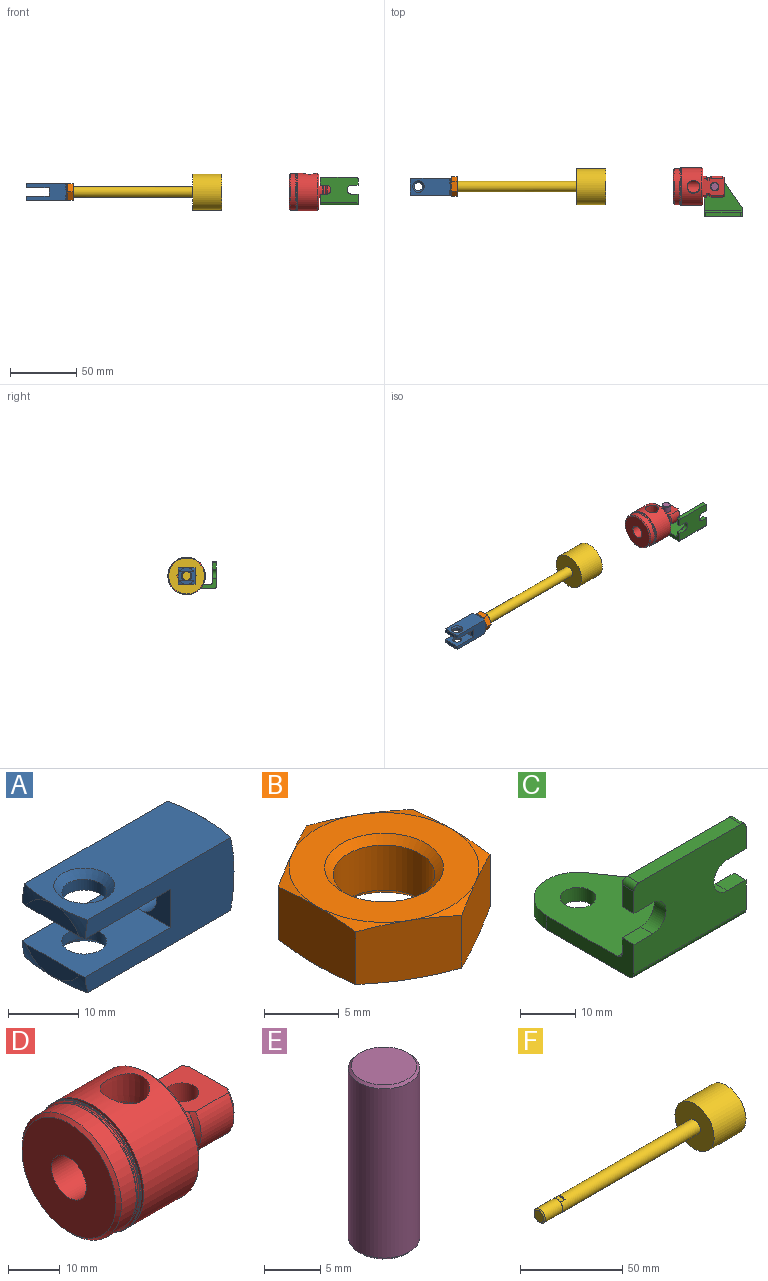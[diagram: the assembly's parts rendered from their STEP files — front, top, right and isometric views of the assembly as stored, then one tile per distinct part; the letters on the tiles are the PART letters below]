
ASSEMBLY  parts=6 mates=5
PART A: 27 faces, bbox 30.5x18.3x18.3 mm
  f0: torus R=3.17mm, axis (1,0,0), area 8.9mm2, adj f3,f5,f9
  f1: plane 30.35x13.05mm, normal (0,-1,0), area 262.9mm2, adj f2,f3,f4,f8,f14,f18,f20,f21
  f2: plane 17.51x12.73mm, normal (0,0,-1), area 189.7mm2, adj f1,f5,f15,f16,f17,f18,f21,f22
  f3: plane 30.18x12.7mm, normal (0,0,1), area 319.9mm2, adj f0,f1,f5,f13,f21,f22,f23
  f4: plane 30.18x12.7mm, normal (0,0,-1), area 319.9mm2, adj f1,f5,f6,f14,f19,f20,f24
  f5: plane 30.35x13.05mm, normal (0,1,0), area 261.5mm2, adj f0,f2,f3,f4,f8,f17,f19,f22
  f6: cone r=3.19mm half-angle=45deg, axis (0,0,-1), area 38.2mm2, adj f4,f7
  f7: cylinder r=3.19mm len=6.39mm, axis (0,0,1), area 37.6mm2, adj f6,f8
  f8: plane 17.51x12.73mm, normal (0,0,1), area 189.7mm2, adj f1,f5,f7,f12,f17,f18,f19,f20
  f9: plane 12.7x12.7mm, normal (1,0,0), area 77.2mm2, adj f0,f11,f14,f23,f24
  f10: cylinder r=3.4mm len=12.13mm, axis (-1,0,0), area 258.8mm2, adj f11,f12,f16,f17,f18
  f11: cone r=3.4mm half-angle=45deg, axis (1,0,0), area 18.7mm2, adj f9,f10
  f12: plane 1.29x0.06mm, normal (1,0,0), area 0.1mm2, adj f8,f10
  f13: cone r=4.34mm half-angle=45deg, axis (0,0,1), area 38.2mm2, adj f3,f15
  f14: torus R=3.17mm, axis (1,0,0), area 8.9mm2, adj f1,f4,f9
  f15: cylinder r=3.19mm len=6.39mm, axis (0,0,1), area 37.6mm2, adj f2,f13
  f16: plane 1.29x0.06mm, normal (1,0,0), area 0.1mm2, adj f2,f10
  f17: plane 6.67x5.7mm, normal (-1,0,0), area 24.3mm2, adj f2,f5,f8,f10
  f18: plane 6.67x5.7mm, normal (-1,0,0), area 24.3mm2, adj f1,f2,f8,f10
  f19: torus R=3.17mm, axis (1,0,0), area 8.2mm2, adj f4,f5,f8,f25
  f20: torus R=3.17mm, axis (1,0,0), area 8.2mm2, adj f1,f4,f8,f25
  f21: torus R=3.17mm, axis (1,0,0), area 8.2mm2, adj f1,f2,f3,f26
  f22: torus R=3.17mm, axis (1,0,0), area 8.2mm2, adj f2,f3,f5,f26
  f23: torus R=3.17mm, axis (1,0,0), area 8.9mm2, adj f1,f3,f9
  f24: torus R=3.17mm, axis (1,0,0), area 8.9mm2, adj f4,f5,f9
  f25: plane 10.81x3.02mm, normal (-1,0,0), area 23mm2, adj f8,f19,f20
  f26: plane 10.81x3.02mm, normal (-1,0,0), area 23mm2, adj f2,f21,f22
PART B: 23 faces, bbox 15.2x15.2x5.4 mm
  f0: plane 6.88x5.36mm, normal (0.5,-0.87,0), area 34.1mm2, adj f1,f6,f8,f10,f18,f19
  f1: plane 6.88x5.36mm, normal (-0.5,-0.87,0), area 34.1mm2, adj f0,f3,f7,f10,f17,f18
  f2: plane 12.7x12.7mm, normal (0,0,-1), area 77.2mm2, adj f7,f8,f9,f10,f12,f13,f15
  f3: cone r=6.35mm half-angle=75deg, axis (0,0,-1), area 3.6mm2, adj f1,f16,f17
  f4: plane 6.88x5.36mm, normal (-0.5,0.87,0), area 34.1mm2, adj f5,f9,f13,f17,f21,f22
  f5: plane 6.88x5.36mm, normal (0.5,0.87,0), area 34.1mm2, adj f4,f6,f12,f13,f20,f21
  f6: plane 7.88x5.37mm, normal (1,0,0), area 34.1mm2, adj f0,f5,f8,f12,f19,f20
  f7: cone r=7.62mm half-angle=75deg, axis (0,0,1), area 3.6mm2, adj f1,f2,f17
  f8: cone r=7.62mm half-angle=75deg, axis (0,0,1), area 3.6mm2, adj f0,f2,f6
  f9: cone r=7.62mm half-angle=75deg, axis (0,0,1), area 3.6mm2, adj f2,f4,f17
  f10: cone r=7.62mm half-angle=75deg, axis (0,0,1), area 3.6mm2, adj f0,f1,f2
  f11: cone r=3.97mm half-angle=45deg, axis (0,0,1), area 18.7mm2, adj f14,f16
  f12: cone r=7.62mm half-angle=75deg, axis (0,0,1), area 3.6mm2, adj f2,f5,f6
  f13: cone r=7.62mm half-angle=75deg, axis (0,0,1), area 3.6mm2, adj f2,f4,f5
  f14: cylinder r=3.4mm len=6.79mm, axis (0,0,1), area 78.5mm2, adj f11,f15
  f15: cone r=3.4mm half-angle=45deg, axis (0,0,-1), area 18.7mm2, adj f2,f14
  f16: plane 12.7x12.7mm, normal (0,0,1), area 77.2mm2, adj f3,f11,f18,f19,f20,f21,f22
  f17: plane 7.88x5.37mm, normal (-1,0,0), area 34.1mm2, adj f1,f3,f4,f7,f9,f22
  f18: cone r=6.35mm half-angle=75deg, axis (0,0,-1), area 3.6mm2, adj f0,f1,f16
  f19: cone r=6.35mm half-angle=75deg, axis (0,0,-1), area 3.6mm2, adj f0,f6,f16
  f20: cone r=6.35mm half-angle=75deg, axis (0,0,-1), area 3.6mm2, adj f5,f6,f16
  f21: cone r=6.35mm half-angle=75deg, axis (0,0,-1), area 3.6mm2, adj f4,f5,f16
  f22: cone r=6.35mm half-angle=75deg, axis (0,0,-1), area 3.6mm2, adj f4,f16,f17
PART C: 22 faces, bbox 28.6x30.2x20.8 mm
  f0: cylinder r=1.27mm len=3.04mm, axis (0,1,0), area 6.1mm2, adj f3,f4,f5,f11
  f1: cylinder r=1.27mm len=3.04mm, axis (0,1,0), area 6.1mm2, adj f3,f4,f5,f10
  f2: plane 4.76x3.04mm, normal (0,0,-1), area 14.5mm2, adj f4,f5,f11,f16
  f3: plane 26.04x3.04mm, normal (0,0,1), area 79.1mm2, adj f0,f1,f4,f5
  f4: plane 28.58x16.44mm, normal (0,1,0), area 366.9mm2, adj f0,f1,f2,f3,f9,f10,f11,f15
  f5: plane 28.58x19.48mm, normal (0,-1,0), area 453.7mm2, adj f0,f1,f2,f3,f6,f10,f11,f15
  f6: cylinder r=1.27mm len=28.58mm, axis (1,0,0), area 57mm2, adj f5,f7,f20,f21
  f7: plane 28.91x28.58mm, normal (0,0,-1), area 581.4mm2, adj f6,f12,f13,f14,f20,f21
  f8: plane 28.58x25.87mm, normal (0,0,1), area 494.6mm2, adj f9,f12,f13,f14,f20,f21
  f9: cylinder r=1.27mm len=28.58mm, axis (1,0,0), area 57mm2, adj f4,f8,f20,f21
  f10: plane 4.86x3.04mm, normal (-1,0,0), area 14.8mm2, adj f1,f4,f5,f17
  f11: plane 4.86x3.04mm, normal (1,0,0), area 14.8mm2, adj f0,f2,f4,f5
  f12: plane 20.39x14.08mm, normal (0.82,0.57,0), area 75.3mm2, adj f7,f8,f13,f21
  f13: cylinder r=7.95mm len=14.49mm, axis (0,0,1), area 61.3mm2, adj f7,f8,f12,f20
  f14: cylinder r=3.21mm len=6.42mm, axis (0,0,1), area 61.3mm2, adj f7,f8
  f15: cylinder r=3.43mm len=6.86mm, axis (0,1,0), area 32.7mm2, adj f4,f5,f17,f18
  f16: cylinder r=3.43mm len=6.86mm, axis (0,1,0), area 32.7mm2, adj f2,f4,f5,f19
  f17: plane 4.76x3.04mm, normal (0,0,-1), area 14.5mm2, adj f4,f5,f10,f15
  f18: plane 4.76x3.04mm, normal (0,0,1), area 14.5mm2, adj f4,f5,f15,f20
  f19: plane 4.76x3.04mm, normal (0,0,1), area 14.5mm2, adj f4,f5,f16,f21
  f20: plane 22.23x7.76mm, normal (-1,0,0), area 81.9mm2, adj f4,f5,f6,f7,f8,f9,f13,f18
  f21: plane 7.76x6.35mm, normal (1,0,0), area 33.6mm2, adj f4,f5,f6,f7,f8,f9,f12,f19
PART D: 41 faces, bbox 38.3x29.1x29.1 mm
  f0: cone r=4.76mm half-angle=60deg, axis (-1,0,0), area 82.3mm2, adj f9
  f1: plane 16.11x12.98mm, normal (0,0,-1), area 160.8mm2, adj f2,f3,f4,f5,f6,f7,f13,f14
  f2: torus R=7.73mm, axis (1,0,0), area 6.8mm2, adj f1,f13,f30,f39
  f3: torus R=7.73mm, axis (1,0,0), area 14.2mm2, adj f1,f13,f17,f30
  f4: cone r=7.1mm half-angle=45deg, axis (1,0,0), area 12.2mm2, adj f1,f5,f30,f39
  f5: cylinder r=7.94mm len=9.46mm, axis (-1,0,0), area 91.3mm2, adj f1,f4,f30,f37
  f6: cylinder r=7.94mm len=9.46mm, axis (-1,0,0), area 91.3mm2, adj f1,f7,f30,f36
  f7: cone r=7.1mm half-angle=45deg, axis (1,0,0), area 12.2mm2, adj f1,f6,f30,f40
  f8: cylinder r=14.11mm len=28.22mm, axis (-1,0,0), area 1258.9mm2, adj f10,f21,f22
  f9: cylinder r=4.76mm len=20.96mm, axis (-1,0,0), area 544.2mm2, adj f0,f11,f34
  f10: cone r=4.62mm half-angle=1.8deg, axis (0,-0.02,1), area 186.3mm2, adj f8,f11
  f11: cylinder r=4.62mm len=9.35mm, axis (0,0.02,-1), area 114.9mm2, adj f9,f10
  f12: cylinder r=14.11mm len=28.22mm, axis (-1,0,0), area 18mm2, adj f24,f28
  f13: cylinder r=6.84mm len=9.46mm, axis (-1,0,0), area 13.4mm2, adj f1,f2,f3,f30
  f14: cylinder r=6.84mm len=9.46mm, axis (-1,0,0), area 13.4mm2, adj f1,f15,f30,f38
  f15: torus R=7.73mm, axis (1,0,0), area 14.2mm2, adj f1,f14,f16,f30
  f16: plane 9.46x1.8mm, normal (1,0,0), area 1.8mm2, adj f1,f15,f18,f30
  f17: plane 9.46x1.8mm, normal (1,0,0), area 1.8mm2, adj f1,f3,f19,f30
  f18: cylinder r=7.91mm len=9.46mm, axis (-1,0,0), area 24.2mm2, adj f1,f16,f20,f30
  f19: cylinder r=7.91mm len=9.46mm, axis (-1,0,0), area 24.2mm2, adj f1,f17,f20,f30
  f20: plane 26.7x26.7mm, normal (1,0,0), area 419.6mm2, adj f1,f18,f19,f21,f30
  f21: cone r=14.11mm half-angle=45deg, axis (-1,0,0), area 93mm2, adj f8,f20
  f22: plane 28.22x28.22mm, normal (-1,0,0), area 57.2mm2, adj f8,f28
  f23: cylinder r=12.85mm len=25.69mm, axis (-1,0,0), area 30.8mm2, adj f27,f31
  f24: plane 28.22x28.22mm, normal (-1,0,0), area 7.4mm2, adj f12,f25
  f25: cone r=14.03mm half-angle=45deg, axis (-1,0,0), area 90mm2, adj f24,f26
  f26: torus R=13.19mm, axis (1,0,0), area 16.5mm2, adj f25,f27
  f27: cone r=13.1mm half-angle=45deg, axis (1,0,0), area 29.8mm2, adj f23,f26
  f28: cone r=13.45mm half-angle=45deg, axis (-1,0,0), area 80.9mm2, adj f12,f22
  f29: cylinder r=3.2mm len=9.46mm, axis (0,0,1), area 190.3mm2, adj f1,f30
  f30: plane 16.11x12.98mm, normal (0,0,1), area 160.8mm2, adj f2,f3,f4,f5,f6,f7,f13,f14
  f31: cone r=13.61mm half-angle=45deg, axis (-1,0,0), area 89.6mm2, adj f23,f32
  f32: cylinder r=13.61mm len=27.22mm, axis (-1,0,0), area 347.5mm2, adj f31,f33
  f33: cone r=12.85mm half-angle=45deg, axis (1,0,0), area 89.6mm2, adj f32,f34
  f34: plane 25.69x25.69mm, normal (-1,0,0), area 447.2mm2, adj f9,f33
  f35: plane 14.2x9.46mm, normal (1,0,0), area 123.6mm2, adj f1,f30,f36,f37
  f36: cone r=7.94mm half-angle=45deg, axis (-1,0,0), area 12.2mm2, adj f1,f6,f30,f35
  f37: cone r=7.94mm half-angle=45deg, axis (-1,0,0), area 12.2mm2, adj f1,f5,f30,f35
  f38: torus R=7.73mm, axis (1,0,0), area 6.8mm2, adj f1,f14,f30,f40
  f39: cone r=7.07mm half-angle=42.3deg, axis (1,0,0), area 0.4mm2, adj f1,f2,f4,f30
  f40: cone r=7.07mm half-angle=42.3deg, axis (1,0,0), area 0.4mm2, adj f1,f7,f30,f38
PART E: 5 faces, bbox 6.4x6.4x19.1 mm
  f0: cone r=3.17mm half-angle=45deg, axis (0,0,1), area 9.5mm2, adj f1,f4
  f1: cylinder r=3.17mm len=18.44mm, axis (0,0,1), area 367.9mm2, adj f0,f2
  f2: cone r=2.92mm half-angle=45deg, axis (0,0,-1), area 6.8mm2, adj f1,f3
  f3: plane 5.85x5.85mm, normal (0,0,1), area 26.9mm2, adj f2
  f4: plane 5.64x5.64mm, normal (0,0,-1), area 25mm2, adj f0
PART F: 12 faces, bbox 130.1x27.1x27.1 mm
  f0: cylinder r=3.96mm len=95.25mm, axis (-1,0,0), area 2339.1mm2, adj f1,f7,f8,f9,f10,f11
  f1: plane 27.11x27.11mm, normal (-1,0,0), area 528.1mm2, adj f0,f2
  f2: cylinder r=13.56mm len=27.11mm, axis (-1,0,0), area 1884.5mm2, adj f1,f3
  f3: plane 27.11x27.11mm, normal (1,0,0), area 577.4mm2, adj f2
  f4: plane 6.68x6.68mm, normal (-1,0,0), area 35mm2, adj f5
  f5: cone r=3.34mm half-angle=45deg, axis (1,0,0), area 20.5mm2, adj f4,f6
  f6: cylinder r=3.97mm len=12.07mm, axis (-1,0,0), area 301mm2, adj f5,f7
  f7: plane 7.94x7.94mm, normal (1,0,0), area 5.2mm2, adj f0,f6,f8,f9
  f8: plane 4.74x3.18mm, normal (0,0,-1), area 15.1mm2, adj f0,f7,f11
  f9: plane 4.74x3.18mm, normal (0,0,1), area 15.1mm2, adj f0,f7,f10
  f10: plane 4.74x0.79mm, normal (-1,0,0), area 2.5mm2, adj f0,f9
  f11: plane 4.74x0.79mm, normal (-1,0,0), area 2.5mm2, adj f0,f8
PLACE A rot(axis=(1,0,0),180deg) t=(-12.27,0,0)mm
PLACE B rot(axis=(0,-1,0),90deg) t=(12.32,0,0)mm
PLACE C t=(202.74,-22.22,-9.47)mm
PLACE D t=(179.73,0,0)mm
PLACE E rot(axis=(1,0,0),180deg) t=(210.69,0,0.05)mm
PLACE F t=(14.73,0,0)mm
MATE fastened A.f10 <-> F.f0  axis (1,0,0) through (11.56,0,0)mm
MATE fastened E.f0 <-> D.f29  axis (0,0,-1) through (210.69,0,0)mm
MATE slider F.f0 <-> D.f0  axis (1,0,0) through (128.93,0,0)mm
MATE fastened F.f0 <-> B.f3  axis (-1,0,0) through (14.73,0,0)mm
MATE revolute C.f13 <-> E.f0  axis (0,0,1) through (210.69,0,-9.47)mm
